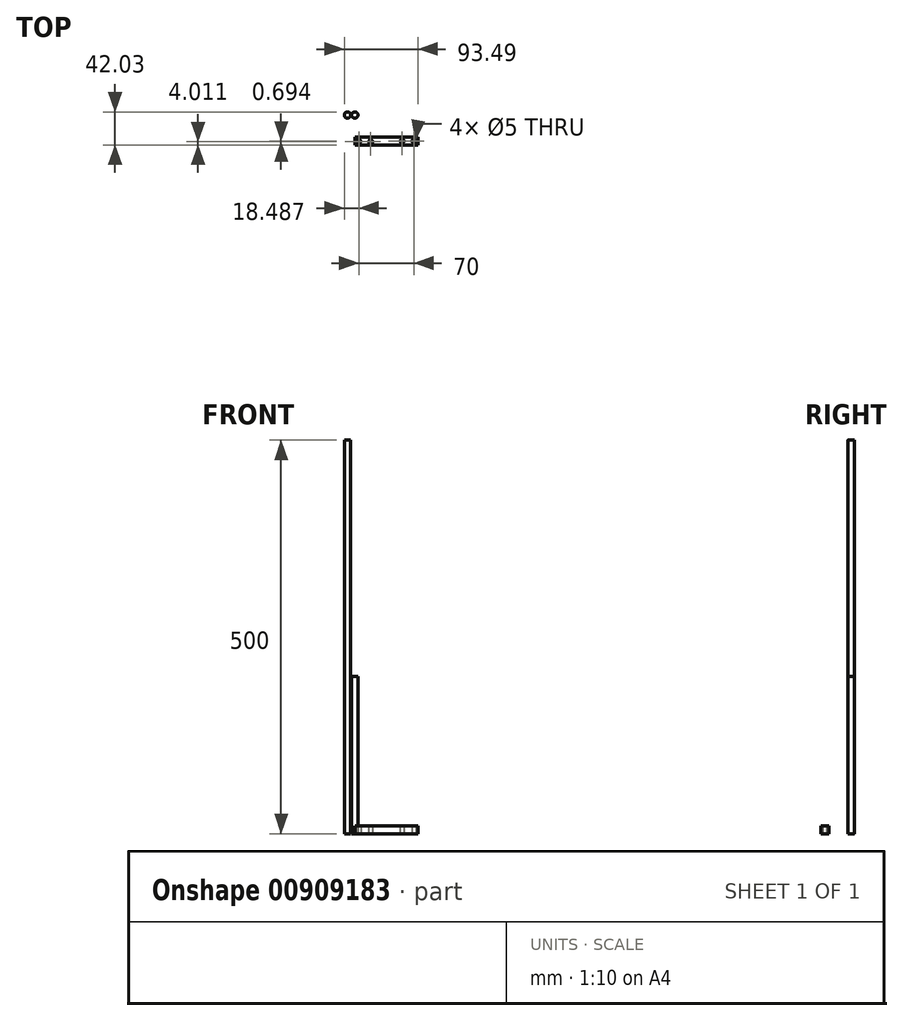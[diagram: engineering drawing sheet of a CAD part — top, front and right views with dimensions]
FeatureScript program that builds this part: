
annotation { "Feature Type Name" : "Feature", "Feature Type Description" : "" }
export const myFeature = defineFeature(function(context is Context, id is Id, definition is map)
    precondition{}
    {
        {
            var Q0;
            Q0=qCreatedBy(makeId("Top.planeOp"),FACE);
            var sketch = newSketch(context, id + "F0", { "sketchPlane" : qUnion([Q0])});
            skCircle(sketch, "E0", {"center": v(0, 0) * mm, "radius": 4 * mm});
            skSolve(sketch);
        }
        {
            var Q0;
            Q0 = qSketchRegion(id + "F0", true);
            extrude(context, id + "F1", {"entities" : qUnion([Q0]), "depth" : 500 * mm, "offsetDistance" : 25 * mm});
        }
        {
            var Q0;
            Q0=qCreatedBy(makeId("Top.planeOp"),FACE);
            var sketch = newSketch(context, id + "F2", { "sketchPlane" : qUnion([Q0])});
            skCircle(sketch, "E1", {"center": v(9.4, 0) * mm, "radius": 4 * mm});
            skSolve(sketch);
        }
        {
            var Q0;
            Q0 = qSketchRegion(id + "F2", true);
            extrude(context, id + "F3", {"entities" : qUnion([Q0]), "depth" : 200 * mm, "offsetDistance" : 25 * mm});
        }
        {
            var Q0;
            Q0=qCreatedBy(makeId("Top.planeOp"),FACE);
            var sketch = newSketch(context, id + "F4", { "sketchPlane" : qUnion([Q0])});
            skLineSegment(sketch, "E2.bottom", {"start": v(9.49, -38.03) * mm, "end": v(89.49, -38.03) * mm});
            skLineSegment(sketch, "E2.top", {"start": v(9.49, -28.03) * mm, "end": v(89.49, -28.03) * mm});
            skLineSegment(sketch, "E2.left", {"start": v(9.49, -38.03) * mm, "end": v(9.49, -28.03) * mm});
            skLineSegment(sketch, "E2.right", {"start": v(89.49, -38.03) * mm, "end": v(89.49, -28.03) * mm});
            skCircle(sketch, "E3", {"center": v(14.49, -33.5) * mm, "radius": 2.5 * mm});
            skCircle(sketch, "E4", {"center": v(29.49, -34.02) * mm, "radius": 2.5 * mm});
            skCircle(sketch, "E5", {"center": v(69.49, -33.33) * mm, "radius": 2.5 * mm});
            skCircle(sketch, "E6", {"center": v(84.49, -33.33) * mm, "radius": 2.5 * mm});
            skSolve(sketch);
        }
        {
            var Q0;
            Q0 = qSketchRegion(id + "F4", true);
            extrude(context, id + "F5", {"entities" : qUnion([Q0]), "depth" : 10 * mm, "offsetDistance" : 25 * mm});
        }
    });
